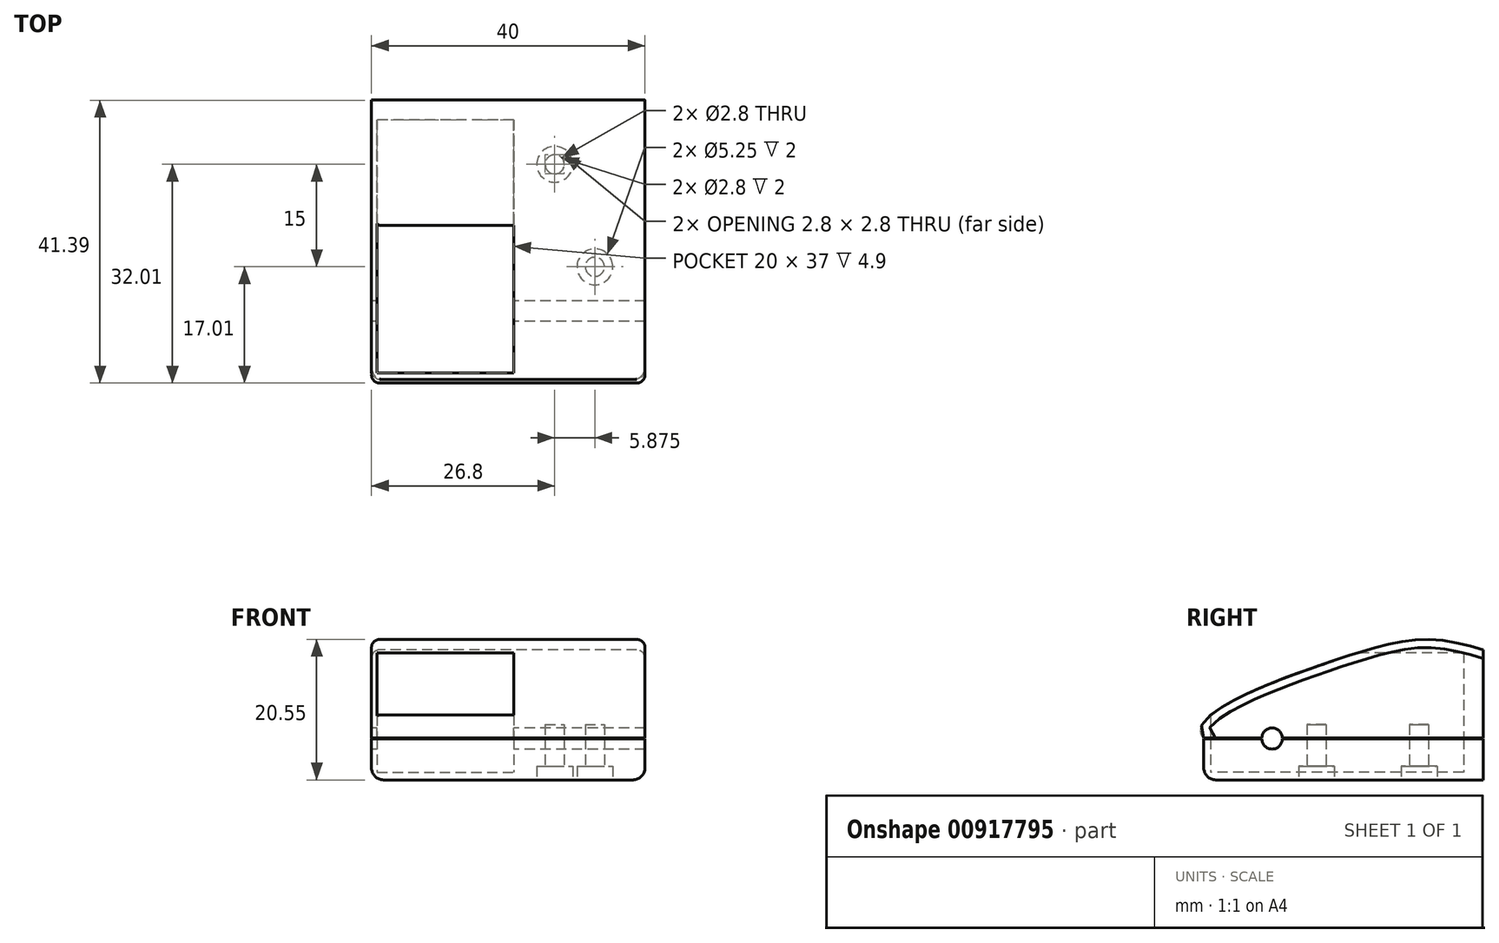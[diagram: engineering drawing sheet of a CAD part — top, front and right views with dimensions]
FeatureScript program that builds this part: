
annotation { "Feature Type Name" : "Feature", "Feature Type Description" : "" }
export const myFeature = defineFeature(function(context is Context, id is Id, definition is map)
    precondition{}
    {
        {
            var Q0;
            Q0=qCreatedBy(makeId("Right.planeOp"),FACE);
            var sketch = newSketch(context, id + "F0", { "sketchPlane" : qUnion([Q0])});
            skLineSegment(sketch, "E0", {"start": v(-45, 0) * mm, "end": v(-36.5, 0) * mm});
            skFitSpline(sketch, "E1", {"points": [v(-45, 0) * mm, v(-24.5, 11.83) * mm, v(-8.25, 14) * mm, v(9.38, 9) * mm, v(21.6, 8) * mm, v(35, 0) * mm, v(-45, 0) * mm]});
            skCircle(sketch, "E2", {"center": v(20, 0) * mm, "radius": 1.5 * mm});
            skCircle(sketch, "E3", {"center": v(-35, 0) * mm, "radius": 1.5 * mm});
            skLineSegment(sketch, "E4.trimOffspring", {"start": v(-33.5, 0) * mm, "end": v(18.5, 0) * mm});
            skLineSegment(sketch, "E5.trimOffspring", {"start": v(21.5, 0) * mm, "end": v(35, 0) * mm});
            skLineSegment(sketch, "E6", {"start": v(-45, -0.1) * mm, "end": v(-36.5, -0.1) * mm});
            skLineSegment(sketch, "E7", {"start": v(35, -0.1) * mm, "end": v(35, -6.1) * mm});
            skLineSegment(sketch, "E8", {"start": v(35, -6.1) * mm, "end": v(-45, -6.1) * mm});
            skLineSegment(sketch, "E9", {"start": v(-45, -6.1) * mm, "end": v(-45, -0.1) * mm});
            skLineSegment(sketch, "E10", {"start": v(-35, 0) * mm, "end": v(-35, -0.1) * mm, "construction": true});
            skLineSegment(sketch, "E11", {"start": v(20, 0) * mm, "end": v(20, -0.1) * mm, "construction": true});
            skCircle(sketch, "E12", {"center": v(-35, -0.1) * mm, "radius": 1.5 * mm});
            skCircle(sketch, "E13", {"center": v(20, -0.1) * mm, "radius": 1.5 * mm});
            skLineSegment(sketch, "E14.trimOffspring", {"start": v(-33.5, -0.1) * mm, "end": v(18.5, -0.1) * mm});
            skLineSegment(sketch, "E15.trimOffspring", {"start": v(21.5, -0.1) * mm, "end": v(35, -0.1) * mm});
            skSolve(sketch);
        }
        {
            var Q0;
            {var subQ1=sQuery(id+"F0.wireOp",EDGE,"E0");Q0=makeQuery(id+"F0.imprint","IMPRINT",FACE,{"disambiguationData":[TD([[makeQuery(id+"F0.imprint","IMPRINT",EDGE,{"derivedFrom":subQ1}),1.0]])]});}
            extrude(context, id + "F1", {"entities" : qUnion([Q0]), "endBound" : BoundingType.SYMMETRIC, "depth" : 40 * mm, "offsetDistance" : 25 * mm});
        }
        {
            var Q0;
            {var subQ0=sQuery(id+"F0.wireOp",EDGE,"E6");Q0=makeQuery(id+"F0.imprint","IMPRINT",FACE,{"disambiguationData":[TD([[makeQuery(id+"F0.imprint","IMPRINT",EDGE,{"derivedFrom":subQ0}),-1.0]])]});}
            extrude(context, id + "F2", {"entities" : qUnion([Q0]), "endBound" : BoundingType.SYMMETRIC, "depth" : 40 * mm, "offsetDistance" : 25 * mm});
        }
        {
            var Q0;
            Q0=makeQuery(id+"F1.opExtrude","CAP_EDGE",EDGE,{"disambiguationData":[OSD([sQuery(id+"F0.wireOp",EDGE,"E1")])],"isStart":false});
            var Q1;
            Q1=makeQuery(id+"F1.opExtrude","CAP_EDGE",EDGE,{"disambiguationData":[OSD([sQuery(id+"F0.wireOp",EDGE,"E1")])],"isStart":true});
            fillet(context, id + "F3", {"entities" : qUnion([Q0, Q1]), "radius" : 1.2 * mm, "tangentPropagation" : true, "allowEdgeOverflow" : false});
        }
        {
            var Q0;
            Q0=makeQuery(id+"F2.opExtrude","CAP_EDGE",EDGE,{"disambiguationData":[OSD([sQuery(id+"F0.wireOp",EDGE,"E8")])],"isStart":false});
            var Q1;
            Q1=makeQuery(id+"F2.opExtrude","CAP_EDGE",EDGE,{"disambiguationData":[OSD([sQuery(id+"F0.wireOp",EDGE,"E8")])],"isStart":true});
            var Q2;
            Q2=makeQuery(id+"F2.opExtrude","SWEPT_EDGE",EDGE,{"disambiguationData":[OSD([sQuery(id+"F0.wireOp",EDGE,"E7"),sQuery(id+"F0.wireOp",EDGE,"E8")])]});
            var Q3;
            Q3=makeQuery(id+"F2.opExtrude","CAP_EDGE",EDGE,{"disambiguationData":[OSD([sQuery(id+"F0.wireOp",EDGE,"E7")])],"isStart":false});
            var Q4;
            Q4=makeQuery(id+"F2.opExtrude","CAP_EDGE",EDGE,{"disambiguationData":[OSD([sQuery(id+"F0.wireOp",EDGE,"E7")])],"isStart":true});
            var Q5;
            Q5=makeQuery(id+"F2.opExtrude","SWEPT_EDGE",EDGE,{"disambiguationData":[OSD([sQuery(id+"F0.wireOp",EDGE,"E8"),sQuery(id+"F0.wireOp",EDGE,"E9")])]});
            var Q6;
            Q6=makeQuery(id+"F2.opExtrude","CAP_EDGE",EDGE,{"disambiguationData":[OSD([sQuery(id+"F0.wireOp",EDGE,"E9")])],"isStart":false});
            var Q7;
            Q7=makeQuery(id+"F2.opExtrude","CAP_EDGE",EDGE,{"disambiguationData":[OSD([sQuery(id+"F0.wireOp",EDGE,"E9")])],"isStart":true});
            fillet(context, id + "F4", {"entities" : qUnion([Q0, Q1, Q2, Q3, Q4, Q5, Q6, Q7]), "radius" : 1.75 * mm, "tangentPropagation" : true, "allowEdgeOverflow" : false});
        }
        {
            var Q0;
            Q0=makeQuery(id+"F1.opExtrude","SWEPT_FACE",FACE,{"disambiguationData":[OSD([sQuery(id+"F0.wireOp",EDGE,"E4.trimOffspring")])]});
            var sketch = newSketch(context, id + "F5", { "sketchPlane" : qUnion([Q0])});
            skLineSegment(sketch, "E16.bottom", {"start": v(-19.2, 7) * mm, "end": v(0.8, 7) * mm});
            skLineSegment(sketch, "E16.top", {"start": v(-19.2, 44) * mm, "end": v(0.8, 44) * mm});
            skLineSegment(sketch, "E16.left", {"start": v(-19.2, 7) * mm, "end": v(-19.2, 44) * mm});
            skLineSegment(sketch, "E16.right", {"start": v(0.8, 7) * mm, "end": v(0.8, 44) * mm});
            skSolve(sketch);
        }
        {
            var Q0;
            Q0=qSketchRegion(id+"F5",true);
            extrude(context, id + "F6", {"entities" : qUnion([Q0]), "operationType" : NewBodyOperationType.REMOVE, "oppositeDirection" : true, "depth" : 12.5 * mm, "offsetDistance" : 25 * mm, "hasSecondDirection" : true, "secondDirectionOppositeDirection" : false, "secondDirectionDepth" : 5 * mm});
        }
        {
            var Q0;
            Q0=makeQuery(id+"F2.opExtrude","SWEPT_FACE",FACE,{"disambiguationData":[OSD([sQuery(id+"F0.wireOp",EDGE,"E8")])]});
            var sketch = newSketch(context, id + "F7", { "sketchPlane" : qUnion([Q0])});
            skLineSegment(sketch, "E17", {"start": v(-6, -27) * mm, "end": v(6, -27) * mm, "construction": true});
            skCircle(sketch, "E18", {"center": v(6, -27) * mm, "radius": 2.62 * mm});
            skCircle(sketch, "E19", {"center": v(6, -27) * mm, "radius": 1.4 * mm});
            skCircle(sketch, "E20", {"center": v(-6, -27) * mm, "radius": 2.62 * mm});
            skCircle(sketch, "E21", {"center": v(-6, -27) * mm, "radius": 1.4 * mm});
            skCircle(sketch, "E22", {"center": v(12.67, 28.5) * mm, "radius": 2.62 * mm});
            skCircle(sketch, "E23", {"center": v(6.8, 13.5) * mm, "radius": 2.62 * mm});
            skCircle(sketch, "E24", {"center": v(6.8, 13.5) * mm, "radius": 1.4 * mm});
            skCircle(sketch, "E25", {"center": v(12.67, 28.5) * mm, "radius": 1.4 * mm});
            skSolve(sketch);
        }
        {
            var Q0;
            Q0=makeQuery(id+"F7.imprint","IMPRINT",FACE,{"disambiguationData":[TD([[makeQuery(id+"F7.imprint","IMPRINT",EDGE,{"derivedFrom":sQuery(id+"F7.wireOp",EDGE,"CFwGyfrO-SKpB-T5sa-KLxF-9wGtCEUgnx70")}),1.0]])]});
            var Q1;
            Q1=makeQuery(id+"F7.imprint","IMPRINT",FACE,{"disambiguationData":[TD([[makeQuery(id+"F7.imprint","IMPRINT",EDGE,{"derivedFrom":sQuery(id+"F7.wireOp",EDGE,"ckw4UnoV-qY22-jN48-Xb4p-lUlQnD4Wo7dg")}),1.0]])]});
            var Q2;
            Q2=makeQuery(id+"F7.imprint","IMPRINT",FACE,{"disambiguationData":[TD([[makeQuery(id+"F7.imprint","IMPRINT",EDGE,{"derivedFrom":sQuery(id+"F7.wireOp",EDGE,"E19")}),1.0]])]});
            var Q3;
            Q3=makeQuery(id+"F7.imprint","IMPRINT",FACE,{"disambiguationData":[TD([[makeQuery(id+"F7.imprint","IMPRINT",EDGE,{"derivedFrom":sQuery(id+"F7.wireOp",EDGE,"E21")}),1.0]])]});
            var Q4;
            Q4=makeQuery(id+"F7.imprint","IMPRINT",FACE,{"disambiguationData":[TD([[makeQuery(id+"F7.imprint","IMPRINT",EDGE,{"derivedFrom":sQuery(id+"F7.wireOp",EDGE,"E24")}),1.0]])]});
            var Q5;
            Q5=makeQuery(id+"F7.imprint","IMPRINT",FACE,{"disambiguationData":[TD([[makeQuery(id+"F7.imprint","IMPRINT",EDGE,{"derivedFrom":sQuery(id+"F7.wireOp",EDGE,"E25")}),1.0]])]});
            extrude(context, id + "F8", {"entities" : qUnion([Q0, Q1, Q2, Q3, Q4, Q5]), "operationType" : NewBodyOperationType.REMOVE, "oppositeDirection" : true, "depth" : 8.1 * mm, "offsetDistance" : 25 * mm});
        }
        {
            var Q0;
            Q0=qSketchRegion(id+"F7",true);
            extrude(context, id + "F9", {"entities" : qUnion([Q0]), "operationType" : NewBodyOperationType.REMOVE, "oppositeDirection" : true, "depth" : 2 * mm, "offsetDistance" : 25 * mm});
        }
        {
            var Q0;
            Q0=qCreatedBy(makeId("Right.planeOp"),FACE);
            var sketch = newSketch(context, id + "F10", { "sketchPlane" : qUnion([Q0])});
            skLineSegment(sketch, "E26.bottom", {"start": v(-4.12, 21.72) * mm, "end": v(61.24, 21.72) * mm});
            skLineSegment(sketch, "E26.top", {"start": v(-4.12, -28.48) * mm, "end": v(61.24, -28.48) * mm});
            skLineSegment(sketch, "E26.left", {"start": v(-4.12, 21.72) * mm, "end": v(-4.12, -28.48) * mm});
            skLineSegment(sketch, "E26.right", {"start": v(61.24, 21.72) * mm, "end": v(61.24, -28.48) * mm});
            skSolve(sketch);
        }
        {
            var Q0;
            Q0 = qSketchRegion(id + "F10", true);
            extrude(context, id + "F11", {"entities" : qUnion([Q0]), "operationType" : NewBodyOperationType.REMOVE, "endBound" : BoundingType.SYMMETRIC, "depth" : 41 * mm, "offsetDistance" : 25 * mm});
        }
    });
